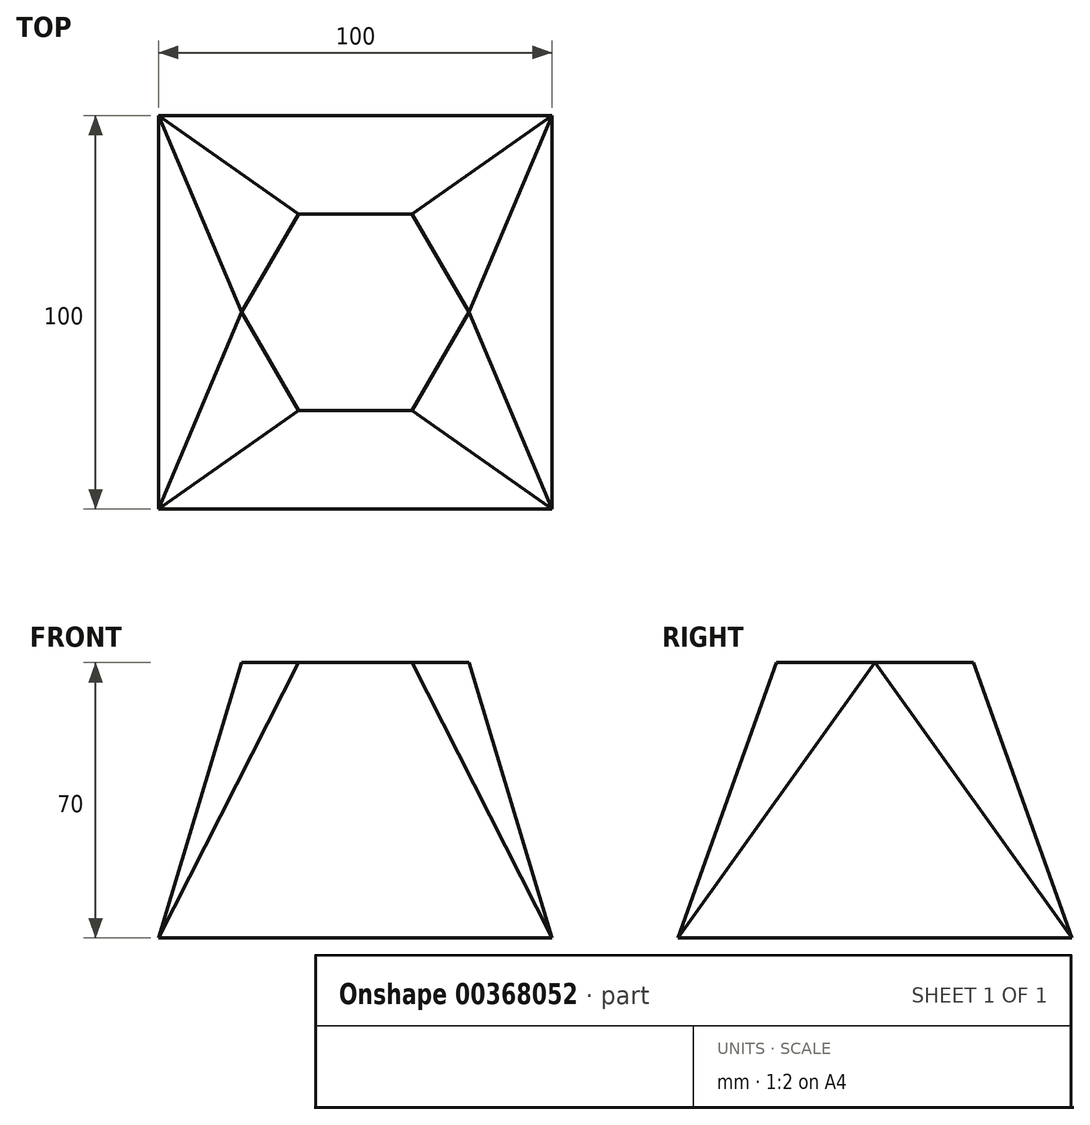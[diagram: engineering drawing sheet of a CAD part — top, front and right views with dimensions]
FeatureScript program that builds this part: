
annotation { "Feature Type Name" : "Feature", "Feature Type Description" : "" }
export const myFeature = defineFeature(function(context is Context, id is Id, definition is map)
    precondition{}
    {
        {
            var Q0;
            Q0=qCreatedBy(makeId("Top.planeOp"),FACE);
            var sketch = newSketch(context, id + "F0", { "sketchPlane" : qUnion([Q0])});
            skLineSegment(sketch, "E0.bottom", {"start": v(50, 50) * mm, "end": v(-50, 50) * mm});
            skLineSegment(sketch, "E0.top", {"start": v(50, -50) * mm, "end": v(-50, -50) * mm});
            skLineSegment(sketch, "E0.left", {"start": v(50, 50) * mm, "end": v(50, -50) * mm});
            skLineSegment(sketch, "E0.right", {"start": v(-50, 50) * mm, "end": v(-50, -50) * mm});
            skPoint(sketch, "E0.middle", {"position": v(0, 0) * mm});
            skSolve(sketch);
        }
        {
            var Q0;
            Q0=qCreatedBy(makeId("Top.planeOp"),FACE);
            cPlane(context, id + "F1", {"entities" : qUnion([Q0]), "cplaneType" : CPlaneType.OFFSET, "offset" : 70 * mm, "width" : 150 * mm, "height" : 150 * mm});
        }
        {
            var Q0;
            Q0=qCreatedBy(id+"F1.planeOp",FACE);
            var sketch = newSketch(context, id + "F2", { "sketchPlane" : qUnion([Q0])});
            skCircle(sketch, "E1.cCircle", {"center": v(0, 0) * mm, "radius": 25 * mm, "construction": true});
            skLineSegment(sketch, "E1.0", {"start": v(-14.43, 25) * mm, "end": v(14.43, 25) * mm});
            skLineSegment(sketch, "E1.1", {"start": v(14.43, 25) * mm, "end": v(28.87, 0) * mm});
            skLineSegment(sketch, "E1.2", {"start": v(28.87, 0) * mm, "end": v(14.43, -25) * mm});
            skLineSegment(sketch, "E1.3", {"start": v(14.43, -25) * mm, "end": v(-14.43, -25) * mm});
            skLineSegment(sketch, "E1.4", {"start": v(-14.43, -25) * mm, "end": v(-28.87, 0) * mm});
            skLineSegment(sketch, "E1.5", {"start": v(-28.87, 0) * mm, "end": v(-14.43, 25) * mm});
            skPoint(sketch, "E1.0.midPoint", {"position": v(0, 25) * mm});
            skLineSegment(sketch, "E2", {"start": v(-14.43, 25) * mm, "end": v(-14.43, -25) * mm});
            skLineSegment(sketch, "E3", {"start": v(14.43, 25) * mm, "end": v(14.43, -25) * mm});
            skSolve(sketch);
        }
        {
            var Q0;
            Q0=makeQuery(id+"F2.imprint","IMPRINT",FACE,{"disambiguationData":[TD([[makeQuery(id+"F2.imprint","IMPRINT",EDGE,{"derivedFrom":sQuery(id+"F2.wireOp",EDGE,"E1.0")}),-1.0]])]});
            var Q1;
            Q1=makeQuery(id+"F0.imprint","IMPRINT",FACE,{"disambiguationData":[TD([[makeQuery(id+"F0.imprint","IMPRINT",EDGE,{"derivedFrom":sQuery(id+"F0.wireOp",EDGE,"E0.bottom")}),1.0]])]});
            loft(context, id + "F3", {"sheetProfilesArray" : [{ "sheetProfileEntities" : qUnion([Q0]) }, { "sheetProfileEntities" : qUnion([Q1]) }]});
        }
        {
            var Q1;
            Q1=makeQuery(id+"F2.imprint","IMPRINT",FACE,{"disambiguationData":[TD([[makeQuery(id+"F2.imprint","IMPRINT",EDGE,{"derivedFrom":sQuery(id+"F2.wireOp",EDGE,"E1.4")}),-1.0]])]});
            var Q2;
            Q2=sQuery(id+"F0.wireOp",VERTEX,"E0.right.start");
            loft(context, id + "F4", {"operationType" : NewBodyOperationType.ADD, "sheetProfilesArray" : [{ "sheetProfileEntities" : qUnion([Q1]) }, { "sheetProfileEntities" : qUnion([Q2]) }]});
        }
        {
            var Q1;
            Q1=makeQuery(id+"F2.imprint","IMPRINT",FACE,{"disambiguationData":[TD([[makeQuery(id+"F2.imprint","IMPRINT",EDGE,{"derivedFrom":sQuery(id+"F2.wireOp",EDGE,"E1.4")}),-1.0]])]});
            var Q2;
            Q2=sQuery(id+"F0.wireOp",VERTEX,"E0.right.end");
            loft(context, id + "F5", {"operationType" : NewBodyOperationType.ADD, "sheetProfilesArray" : [{ "sheetProfileEntities" : qUnion([Q1]) }, { "sheetProfileEntities" : qUnion([Q2]) }]});
        }
        {
            var Q1;
            Q1=makeQuery(id+"F2.imprint","IMPRINT",FACE,{"disambiguationData":[TD([[makeQuery(id+"F2.imprint","IMPRINT",EDGE,{"derivedFrom":sQuery(id+"F2.wireOp",EDGE,"E1.1")}),-1.0]])]});
            var Q2;
            Q2=sQuery(id+"F0.wireOp",VERTEX,"E0.left.end");
            loft(context, id + "F6", {"operationType" : NewBodyOperationType.ADD, "sheetProfilesArray" : [{ "sheetProfileEntities" : qUnion([Q1]) }, { "sheetProfileEntities" : qUnion([Q2]) }]});
        }
        {
            var Q1;
            Q1=makeQuery(id+"F2.imprint","IMPRINT",FACE,{"disambiguationData":[TD([[makeQuery(id+"F2.imprint","IMPRINT",EDGE,{"derivedFrom":sQuery(id+"F2.wireOp",EDGE,"E1.1")}),-1.0]])]});
            var Q2;
            Q2=sQuery(id+"F0.wireOp",VERTEX,"E0.left.start");
            loft(context, id + "F7", {"operationType" : NewBodyOperationType.ADD, "sheetProfilesArray" : [{ "sheetProfileEntities" : qUnion([Q1]) }, { "sheetProfileEntities" : qUnion([Q2]) }]});
        }
        {
            var Q1;
            Q1=makeQuery(id+"F6.opLoft","SWEPT_FACE",FACE,{"disambiguationData":[OSD([sQuery(id+"F2.wireOp",EDGE,"E1.0"),sQuery(id+"F2.wireOp",EDGE,"E1.1"),sQuery(id+"F2.wireOp",EDGE,"E1.2"),sQuery(id+"F2.wireOp",EDGE,"E3")])]});
            var Q2;
            Q2=makeQuery(id+"F7.opLoft","SWEPT_FACE",FACE,{"disambiguationData":[OSD([sQuery(id+"F2.wireOp",EDGE,"E1.1"),sQuery(id+"F2.wireOp",EDGE,"E1.2"),sQuery(id+"F2.wireOp",EDGE,"E1.3"),sQuery(id+"F2.wireOp",EDGE,"E3")])]});
            var Q3;
            Q3=sQuery(id+"F0.wireOp",VERTEX,"E0.left.end");
            var Q4;
            Q4=sQuery(id+"F0.wireOp",VERTEX,"E0.bottom.start");
            loft(context, id + "F8", {"operationType" : NewBodyOperationType.ADD, "sheetProfilesArray" : [{ "sheetProfileEntities" : qUnion([Q1]) }, { "sheetProfileEntities" : qUnion([Q2]) }], "matchConnections" : true, "connections" : [{ "connectionEntities" : qUnion([Q3, Q4]), "connectionEdgeQueries" : qUnion([]), "connectionEdgeParameters" : [] }]});
        }
        {
            var Q1;
            Q1=makeQuery(id+"F4.opLoft","SWEPT_FACE",FACE,{"disambiguationData":[OSD([sQuery(id+"F2.wireOp",EDGE,"E1.3"),sQuery(id+"F2.wireOp",EDGE,"E1.4"),sQuery(id+"F2.wireOp",EDGE,"E1.5"),sQuery(id+"F2.wireOp",EDGE,"E2")])]});
            var Q2;
            Q2=makeQuery(id+"F5.opLoft","SWEPT_FACE",FACE,{"disambiguationData":[OSD([sQuery(id+"F2.wireOp",EDGE,"E1.0"),sQuery(id+"F2.wireOp",EDGE,"E1.4"),sQuery(id+"F2.wireOp",EDGE,"E1.5"),sQuery(id+"F2.wireOp",EDGE,"E2")])]});
            var Q3;
            Q3=sQuery(id+"F0.wireOp",VERTEX,"E0.bottom.end");
            var Q4;
            Q4=sQuery(id+"F0.wireOp",VERTEX,"E0.right.end");
            loft(context, id + "F9", {"operationType" : NewBodyOperationType.ADD, "sheetProfilesArray" : [{ "sheetProfileEntities" : qUnion([Q1]) }, { "sheetProfileEntities" : qUnion([Q2]) }], "matchConnections" : true, "connections" : [{ "connectionEntities" : qUnion([Q3, Q4]), "connectionEdgeQueries" : qUnion([]), "connectionEdgeParameters" : [] }]});
        }
    });
